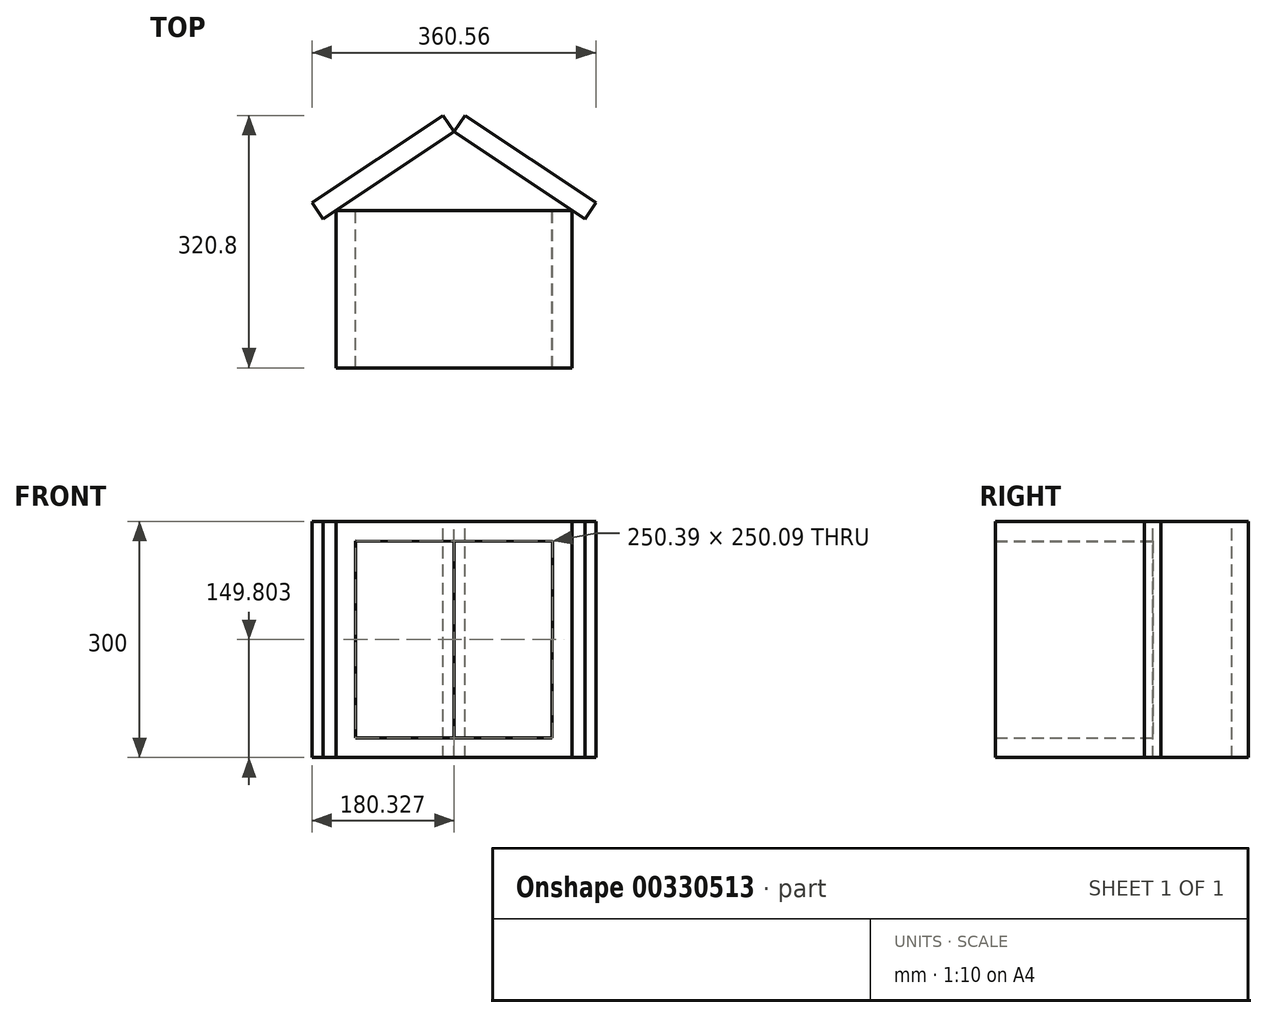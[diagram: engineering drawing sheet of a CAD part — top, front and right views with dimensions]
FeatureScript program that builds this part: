
annotation { "Feature Type Name" : "Feature", "Feature Type Description" : "" }
export const myFeature = defineFeature(function(context is Context, id is Id, definition is map)
    precondition{}
    {
        {
            var Q0;
            Q0=qCreatedBy(makeId("Front.planeOp"),FACE);
            var sketch = newSketch(context, id + "F0", { "sketchPlane" : qUnion([Q0])});
            skLineSegment(sketch, "E0.bottom", {"start": v(250.16, -25) * mm, "end": v(-49.84, -25) * mm});
            skLineSegment(sketch, "E0.top", {"start": v(250.16, 275) * mm, "end": v(-49.84, 275) * mm});
            skLineSegment(sketch, "E0.left", {"start": v(250.16, -25) * mm, "end": v(250.16, 275) * mm});
            skLineSegment(sketch, "E0.right", {"start": v(-49.84, -25) * mm, "end": v(-49.84, 275) * mm});
            skLineSegment(sketch, "E1", {"start": v(100.16, 275) * mm, "end": v(100.16, 250) * mm});
            skLineSegment(sketch, "E2", {"start": v(-49.84, 125) * mm, "end": v(-24.84, 125) * mm});
            skPoint(sketch, "E2.endSnap0", {"position": v(-49.84, 125) * mm});
            skLineSegment(sketch, "E3", {"start": v(-49.84, 275) * mm, "end": v(-24.99, 249.85) * mm});
            skLineSegment(sketch, "E4", {"start": v(250.16, 275) * mm, "end": v(225.4, 249.76) * mm});
            skLineSegment(sketch, "E5", {"start": v(250.16, -25) * mm, "end": v(225, -0.15) * mm});
            skLineSegment(sketch, "E6", {"start": v(-24.6, -0.24) * mm, "end": v(-49.84, -25) * mm});
            skLineSegment(sketch, "E7", {"start": v(250.16, 125) * mm, "end": v(225.16, 125) * mm});
            skPoint(sketch, "E7.endSnap0", {"position": v(250.16, 125) * mm});
            skLineSegment(sketch, "E8", {"start": v(100.16, -25) * mm, "end": v(100.16, 0) * mm});
            skLineSegment(sketch, "E9", {"start": v(225.4, 249.76) * mm, "end": v(225, -0.15) * mm});
            skLineSegment(sketch, "E10", {"start": v(225, -0.15) * mm, "end": v(-24.6, -0.24) * mm});
            skLineSegment(sketch, "E11", {"start": v(-24.6, -0.24) * mm, "end": v(-24.99, 249.85) * mm});
            skLineSegment(sketch, "E12", {"start": v(-24.99, 249.85) * mm, "end": v(225.4, 249.76) * mm});
            skSolve(sketch);
        }
        {
            var Q0;
            {var subQ1=sQuery(id+"F0.wireOp",EDGE,"E3");Q0=makeQuery(id+"F0.imprint","IMPRINT",FACE,{"disambiguationData":[TD([[makeQuery(id+"F0.imprint","IMPRINT",EDGE,{"derivedFrom":subQ1}),1.0]])]});}
            var Q1;
            {var subQ0=sQuery(id+"F0.wireOp",EDGE,"E4");Q1=makeQuery(id+"F0.imprint","IMPRINT",FACE,{"disambiguationData":[TD([[makeQuery(id+"F0.imprint","IMPRINT",EDGE,{"derivedFrom":subQ0}),1.0]])]});}
            var Q2;
            {var subQ0=sQuery(id+"F0.wireOp",EDGE,"E5");Q2=makeQuery(id+"F0.imprint","IMPRINT",FACE,{"disambiguationData":[TD([[makeQuery(id+"F0.imprint","IMPRINT",EDGE,{"derivedFrom":subQ0}),-1.0]])]});}
            var Q3;
            {var subQ0=sQuery(id+"F0.wireOp",EDGE,"E5");Q3=makeQuery(id+"F0.imprint","IMPRINT",FACE,{"disambiguationData":[TD([[makeQuery(id+"F0.imprint","IMPRINT",EDGE,{"derivedFrom":subQ0}),1.0]])]});}
            var Q4;
            {var subQ0=sQuery(id+"F0.wireOp",EDGE,"E6");Q4=makeQuery(id+"F0.imprint","IMPRINT",FACE,{"disambiguationData":[TD([[makeQuery(id+"F0.imprint","IMPRINT",EDGE,{"derivedFrom":subQ0}),1.0]])]});}
            var Q5;
            {var subQ0=sQuery(id+"F0.wireOp",EDGE,"E3");Q5=makeQuery(id+"F0.imprint","IMPRINT",FACE,{"disambiguationData":[TD([[makeQuery(id+"F0.imprint","IMPRINT",EDGE,{"derivedFrom":subQ0}),-1.0]])]});}
            extrude(context, id + "F1", {"entities" : qUnion([Q0, Q1, Q2, Q3, Q4, Q5]), "depth" : 200 * mm});
        }
        {
            var Q0;
            Q0=makeQuery(id+"F1.opExtrude","SWEPT_FACE",FACE,{"disambiguationData":[OSD([sQuery(id+"F0.wireOp",EDGE,"E0.top")])]});
            var sketch = newSketch(context, id + "F2", { "sketchPlane" : qUnion([Q0])});
            skLineSegment(sketch, "E13", {"start": v(100.16, 0) * mm, "end": v(100.16, 100) * mm});
            skPoint(sketch, "E13.endSnap0", {"position": v(100.16, 0) * mm});
            skLineSegment(sketch, "E14", {"start": v(-49.84, 0) * mm, "end": v(100.16, 100) * mm});
            skLineSegment(sketch, "E15", {"start": v(250.16, 0) * mm, "end": v(100.16, 100) * mm});
            skLineSegment(sketch, "E16", {"start": v(100.16, 100) * mm, "end": v(86.3, 120.8) * mm});
            skLineSegment(sketch, "E17", {"start": v(86.3, 120.8) * mm, "end": v(-80.12, 9.86) * mm});
            skLineSegment(sketch, "E18", {"start": v(100.16, 100) * mm, "end": v(114.03, 120.8) * mm});
            skLineSegment(sketch, "E19", {"start": v(114.03, 120.8) * mm, "end": v(280.44, 9.86) * mm});
            skLineSegment(sketch, "E20", {"start": v(280.44, 9.86) * mm, "end": v(266.57, -10.94) * mm});
            skLineSegment(sketch, "E21", {"start": v(266.57, -10.94) * mm, "end": v(250.16, 0) * mm});
            skLineSegment(sketch, "E22", {"start": v(-80.12, 9.86) * mm, "end": v(-66.25, -10.94) * mm});
            skLineSegment(sketch, "E23", {"start": v(-66.25, -10.94) * mm, "end": v(-49.84, 0) * mm});
            skLineSegment(sketch, "E24", {"start": v(-49.84, 0) * mm, "end": v(100.16, 0) * mm});
            skLineSegment(sketch, "E25", {"start": v(-49.84, 0) * mm, "end": v(-24.84, 0) * mm});
            skLineSegment(sketch, "E26", {"start": v(100.16, 0) * mm, "end": v(-24.84, 0) * mm});
            skSolve(sketch);
        }
        {
            var Q0;
            Q0=makeQuery(id+"F2.imprint","IMPRINT",FACE,{"disambiguationData":[TD([[makeQuery(id+"F2.imprint","IMPRINT",EDGE,{"derivedFrom":sQuery(id+"F2.wireOp",EDGE,"E14")}),1.0]])]});
            var Q1;
            Q1=makeQuery(id+"F2.imprint","IMPRINT",FACE,{"disambiguationData":[TD([[makeQuery(id+"F2.imprint","IMPRINT",EDGE,{"derivedFrom":sQuery(id+"F2.wireOp",EDGE,"E15")}),-1.0]])]});
            extrude(context, id + "F3", {"entities" : qUnion([Q0, Q1]), "oppositeDirection" : true, "depth" : 300 * mm});
        }
    });
